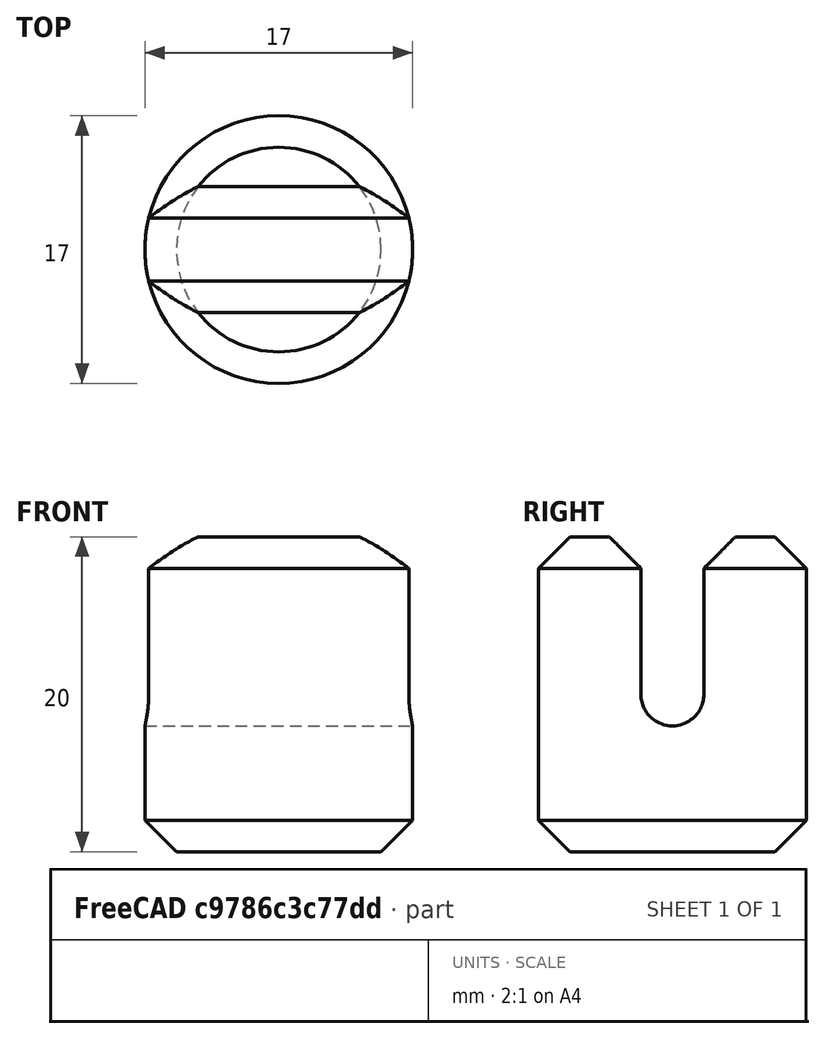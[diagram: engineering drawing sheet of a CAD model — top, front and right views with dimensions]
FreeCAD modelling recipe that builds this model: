
FCSTD DOCUMENT  (FreeCAD 0.17R13522 (Git))
Label: plug
License: All rights reserved
LicenseURL: http://en.wikipedia.org/wiki/All_rights_reserved
objects: Part::Cylinder×2, Part::Box×1, Part::MultiFuse×1, Part::Cut×1, Part::Chamfer×1
note: 6 computed .brp shape members not serialized (recipe doc carries the construction recipe); baked Part::Feature solids carry a one-line shape summary decoded from their .brp

FEATURE [Part::Cylinder] Cylinder
  Angle = 360
  AttacherType = Attacher::AttachEngine3D
  Height = 20
  Radius = 8.5
FEATURE [Part::Cylinder] Cylinder001
  Angle = 360
  AttacherType = Attacher::AttachEngine3D
  Height = 20
  Placement = pos=(-10,0,10) rot=(0,1,0;1.5708rad)
  Radius = 2
FEATURE [Part::Box] Box  label="Cube"
  AttacherType = Attacher::AttachEngine3D
  Height = 10
  Length = 20
  Placement = pos=(-10,-2,10) rot=(0,0,1;0rad)
  Width = 4
FEATURE [Part::MultiFuse] Fusion
  Shapes = -> [Cylinder001,Box]
FEATURE [Part::Cut] Cut
  Base = -> Cylinder
  Tool = -> Fusion
FEATURE [Part::Chamfer] Chamfer
  Base = -> Cut
  Edges = 5 edges r=2: [Edge1,Edge6,Edge10,Edge13,Edge17]
